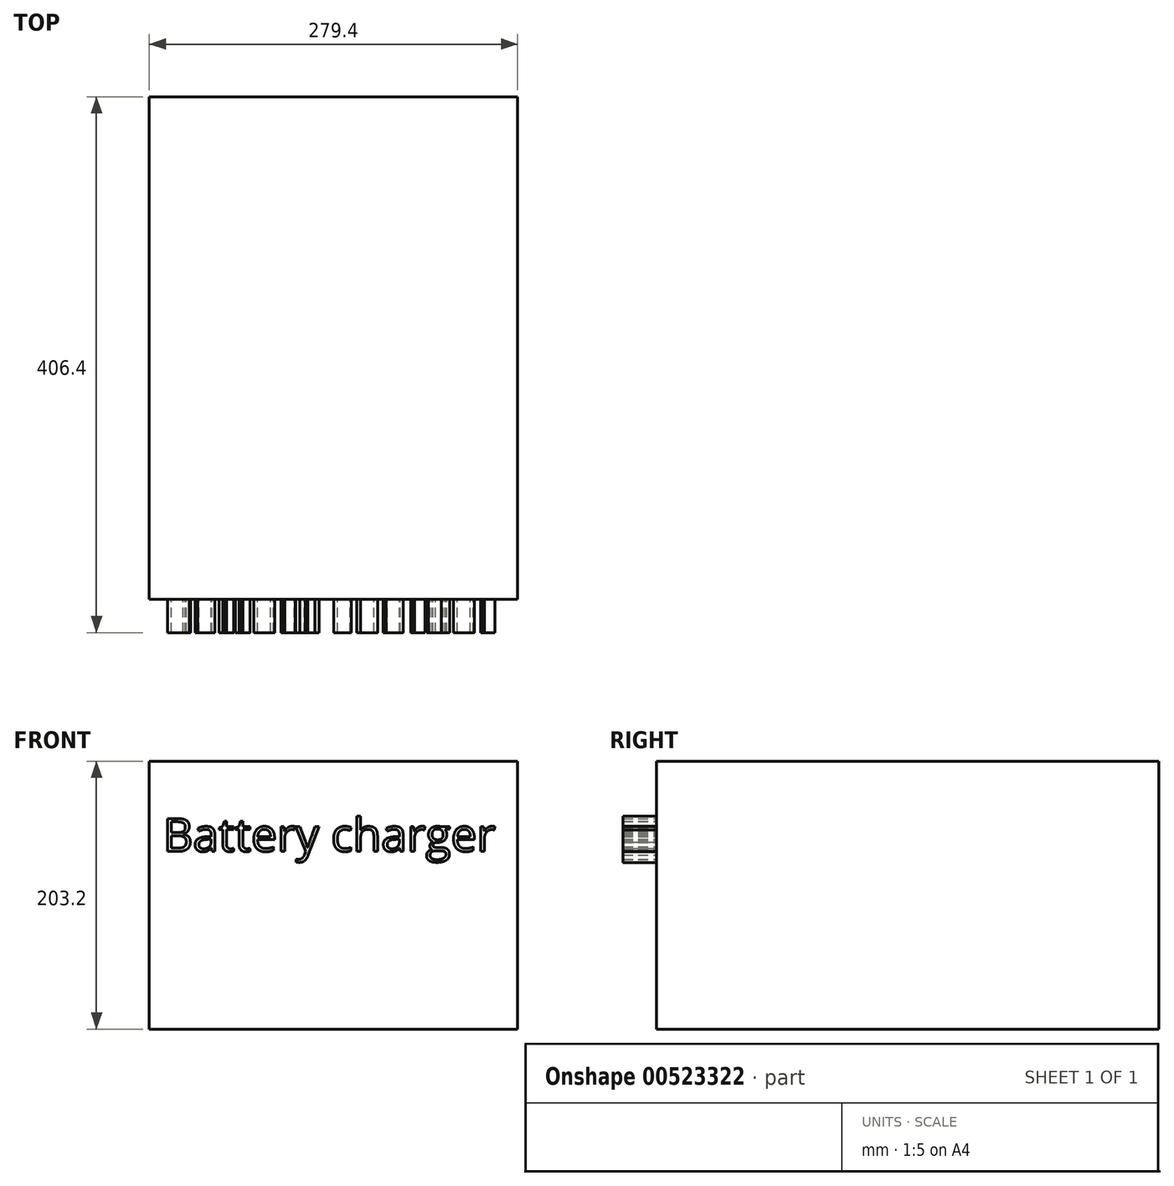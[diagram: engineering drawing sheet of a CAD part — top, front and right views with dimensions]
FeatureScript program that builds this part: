
annotation { "Feature Type Name" : "Feature", "Feature Type Description" : "" }
export const myFeature = defineFeature(function(context is Context, id is Id, definition is map)
    precondition{}
    {
        {
            var Q0;
            Q0=qCreatedBy(makeId("Front.planeOp"),FACE);
            var sketch = newSketch(context, id + "F0", { "sketchPlane" : qUnion([Q0])});
            skLineSegment(sketch, "E0.bottom", {"start": v(-139.7, 101.6) * mm, "end": v(139.7, 101.6) * mm});
            skLineSegment(sketch, "E0.top", {"start": v(-139.7, -101.6) * mm, "end": v(139.7, -101.6) * mm});
            skLineSegment(sketch, "E0.left", {"start": v(-139.7, 101.6) * mm, "end": v(-139.7, -101.6) * mm});
            skLineSegment(sketch, "E0.right", {"start": v(139.7, 101.6) * mm, "end": v(139.7, -101.6) * mm});
            skPoint(sketch, "E0.middle", {"position": v(0, 0) * mm});
            skSolve(sketch);
        }
        {
            var Q0;
            Q0=makeQuery(id+"F0.imprint","IMPRINT",FACE,{"disambiguationData":[TD([[makeQuery(id+"F0.imprint","IMPRINT",EDGE,{"derivedFrom":sQuery(id+"F0.wireOp",EDGE,"E0.bottom")}),-1.0]])]});
            extrude(context, id + "F1", {"entities" : qUnion([Q0]), "depth" : 381 * mm, "offsetDistance" : 25.4 * mm});
        }
        {
            var Q0;
            Q0=makeQuery(id+"F1.opExtrude","CAP_FACE",FACE,{"disambiguationData":[OSD([sQuery(id+"F0.wireOp",EDGE,"E0.bottom"),sQuery(id+"F0.wireOp",EDGE,"E0.top"),sQuery(id+"F0.wireOp",EDGE,"E0.left"),sQuery(id+"F0.wireOp",EDGE,"E0.right")])],"isStart":false});
            var sketch = newSketch(context, id + "F2", { "sketchPlane" : qUnion([Q0])});
            skText(sketch, "E1", { "text": "Battery charger", "fontName": "OpenSans-Regular.ttf"});
            const initialGuessF2  = {"E1": [-0.12923, 0.03318, 1, 0, 0.02517]};
            skSetInitialGuess(sketch, initialGuessF2);
            skSolve(sketch);
        }
        {
            var Q0;
            Q0 = qSketchRegion(id + "F2", true);
            extrude(context, id + "F3", {"entities" : qUnion([Q0]), "operationType" : NewBodyOperationType.ADD, "depth" : 25.4 * mm, "offsetDistance" : 25.4 * mm});
        }
    });
